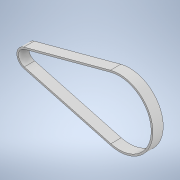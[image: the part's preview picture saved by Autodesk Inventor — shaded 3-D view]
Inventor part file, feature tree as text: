
AUTODESK INVENTOR PART (.ipt)
format: ipt  version: 2020.3 (Build 243373000, 373)  size: 115,712 bytes
history: native  units: mm
features: extrude x1, sketch x1
ambient origin geometry x8: Origin, YZ Plane, XZ Plane, XY Plane, X Axis, Y Axis, Z Axis, Center Point
bodies: Solid1 (feature_tree)
feature tree (2):
  extrude  "Extrusion1"  Depth=6.0mm
  sketch  "Sketch1"  dims[d0=5.095541mm d1=19.10828mm d9=54.0mm d10=0.5mm d11=0.5mm d12=6.0mm d13=0.0mm]
